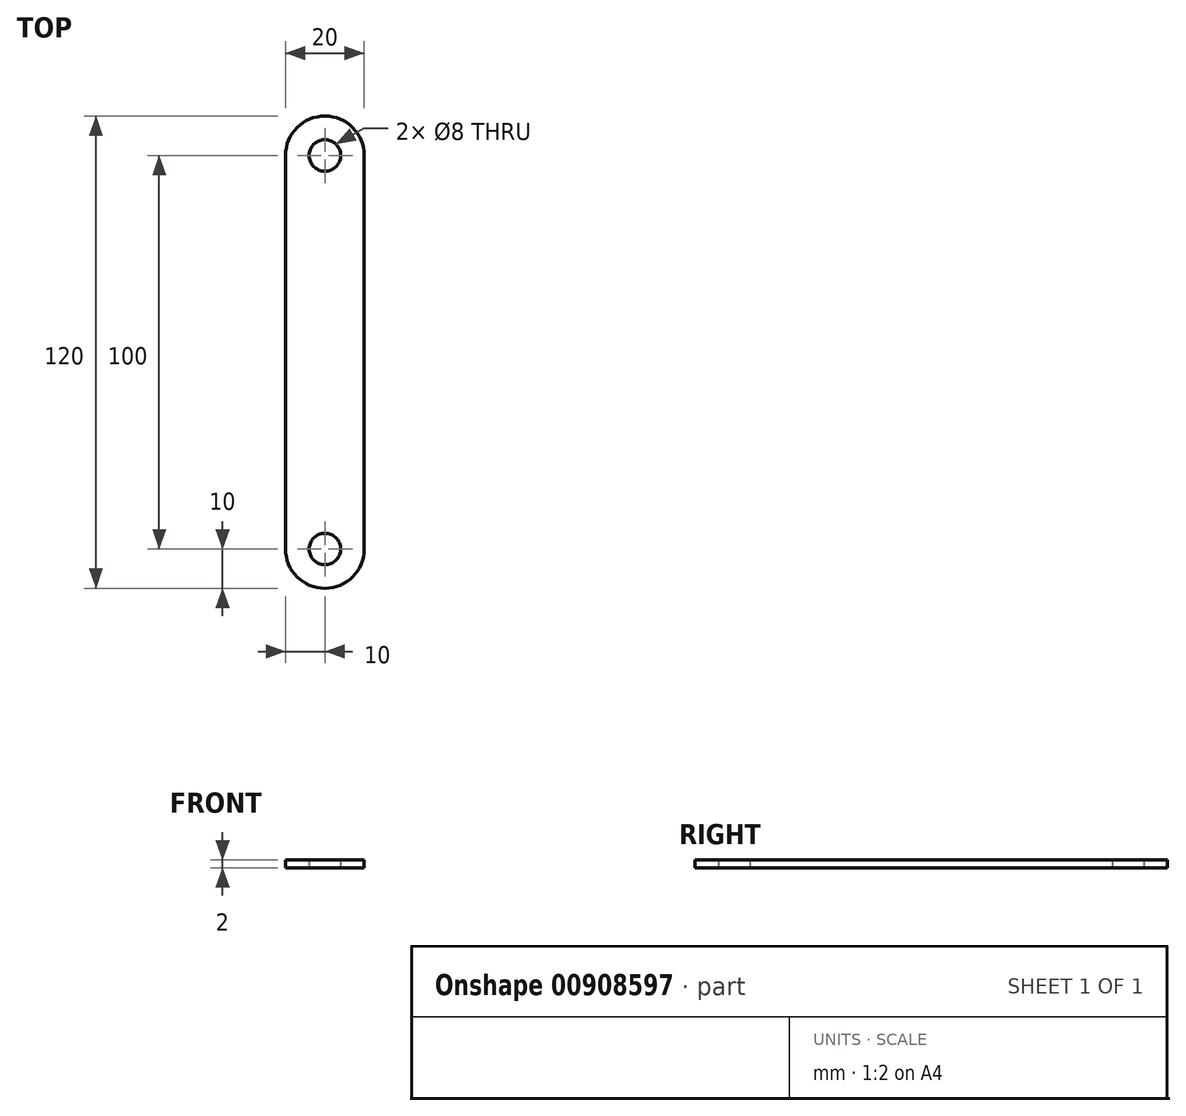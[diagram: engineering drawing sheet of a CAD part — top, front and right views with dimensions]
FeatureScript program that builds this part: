
annotation { "Feature Type Name" : "Feature", "Feature Type Description" : "" }
export const myFeature = defineFeature(function(context is Context, id is Id, definition is map)
    precondition{}
    {
        {
            var Q0;
            Q0=qCreatedBy(makeId("Top.planeOp"),FACE);
            var sketch = newSketch(context, id + "F0", { "sketchPlane" : qUnion([Q0])});
            skLineSegment(sketch, "E0.bottom", {"start": v(10, 100) * mm, "end": v(-10, 100) * mm});
            skLineSegment(sketch, "E0.top", {"start": v(10, -100) * mm, "end": v(-10, -100) * mm});
            skLineSegment(sketch, "E0.left", {"start": v(10, 100) * mm, "end": v(10, -100) * mm});
            skLineSegment(sketch, "E0.right", {"start": v(-10, 100) * mm, "end": v(-10, -100) * mm});
            skPoint(sketch, "E0.middle", {"position": v(0, 0) * mm});
            skArc(sketch, "E1", {"start": v(-10, 100) * mm, "mid": v(0, 110) * mm, "end": v(10, 100) * mm});
            skArc(sketch, "E2.MirrorCS", {"start": v(-10, -100) * mm, "mid": v(0, -110) * mm, "end": v(10, -100) * mm});
            skSolve(sketch);
        }
        {
            var Q0;
            Q0=qSketchRegion(id+"F0",true);
            extrude(context, id + "F1", {"entities" : qUnion([Q0]), "depth" : 2 * mm, "offsetDistance" : 25 * mm});
        }
        {
            var Q0;
            Q0=qCreatedBy(makeId("Top.planeOp"),FACE);
            var sketch = newSketch(context, id + "F2", { "sketchPlane" : qUnion([Q0])});
            skCircle(sketch, "E3", {"center": v(0, 100) * mm, "radius": 4 * mm});
            skCircle(sketch, "E4", {"center": v(0, 0) * mm, "radius": 4 * mm});
            skCircle(sketch, "E5.MirrorC", {"center": v(0, -100) * mm, "radius": 4 * mm});
            skSolve(sketch);
        }
        {
            var Q0;
            Q0=qSketchRegion(id+"F2",true);
            extrude(context, id + "F3", {"entities" : qUnion([Q0]), "operationType" : NewBodyOperationType.REMOVE, "endBound" : BoundingType.SYMMETRIC, "depth" : 25 * mm, "offsetDistance" : 25 * mm});
        }
        {
            var Q0;
            Q0=makeQuery(id+"F1.opExtrude","CAP_FACE",FACE,{"disambiguationData":[OSD([sQuery(id+"F0.wireOp",EDGE,"E0.left"),sQuery(id+"F0.wireOp",EDGE,"E0.right"),sQuery(id+"F0.wireOp",EDGE,"E1"),sQuery(id+"F0.wireOp",EDGE,"E2.MirrorCS")])],"isStart":false});
            var sketch = newSketch(context, id + "F4", { "sketchPlane" : qUnion([Q0])});
            skCircle(sketch, "E6", {"center": v(0, 0) * mm, "radius": 6 * mm});
            skCircle(sketch, "E7.0", {"center": v(0, 0) * mm, "radius": 4 * mm});
            skSolve(sketch);
        }
        {
            var Q0;
            Q0=qSketchRegion(id+"F4",true);
            extrude(context, id + "F5", {"entities" : qUnion([Q0]), "depth" : 2 * mm, "offsetDistance" : 25 * mm});
        }
        {
            var Q0;
            Q0=makeQuery(id+"F5.opExtrude","SWEPT_BODY",BODY,{"disambiguationData":[OSD([sQuery(id+"F4.wireOp",EDGE,"E6"),sQuery(id+"F4.wireOp",EDGE,"E7.0")])]});
            deleteBodies(context, id + "F6", {"entities" : qUnion([Q0])});
        }
        {
            var Q0;
            Q0=makeQuery(id+"F1.opExtrude","CAP_FACE",FACE,{"disambiguationData":[OSD([sQuery(id+"F0.wireOp",EDGE,"E0.left"),sQuery(id+"F0.wireOp",EDGE,"E0.right"),sQuery(id+"F0.wireOp",EDGE,"E1"),sQuery(id+"F0.wireOp",EDGE,"E2.MirrorCS")])],"isStart":false});
            var sketch = newSketch(context, id + "F7", { "sketchPlane" : qUnion([Q0])});
            skArc(sketch, "E8", {"start": v(-10, 0) * mm, "mid": v(0, -10) * mm, "end": v(10, 0) * mm});
            skLineSegment(sketch, "E9.0", {"start": v(10, 0) * mm, "end": v(10, -100) * mm});
            skLineSegment(sketch, "E10.0", {"start": v(-10, 0) * mm, "end": v(-10, -100) * mm});
            skArc(sketch, "E11.0", {"start": v(-10, -100) * mm, "mid": v(0, -110) * mm, "end": v(10, -100) * mm});
            skPoint(sketch, "E12.orphan", {"position": v(10, 100) * mm});
            skPoint(sketch, "E13.orphan", {"position": v(-10, 100) * mm});
            skSolve(sketch);
        }
        {
            var Q0;
            Q0 = qSketchRegion(id + "F7", true);
            extrude(context, id + "F8", {"entities" : qUnion([Q0]), "operationType" : NewBodyOperationType.REMOVE, "oppositeDirection" : true, "depth" : 25 * mm, "offsetDistance" : 25 * mm});
        }
    });
